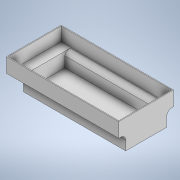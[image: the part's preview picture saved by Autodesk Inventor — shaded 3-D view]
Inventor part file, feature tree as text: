
AUTODESK INVENTOR PART (.ipt)
format: ipt  version: 2020.1 (Build 241239000, 239)  size: 161,792 bytes
history: native  units: mm
features: extrude x4, sketch x4, projected_geometry x4, other x1, fillet x1, shell x1
ambient origin geometry x8: Origin, YZ Plane, XZ Plane, XY Plane, X Axis, Y Axis, Z Axis, Center Point
bodies: Body1 (feature_tree)
feature tree (15):
  other  "Твердое тело1"
  extrude  "Выдавливание1"  Depth=142.0mm
  fillet  "Сопряжение1"  Radius=190.0mm
  extrude  "Выдавливание2"  Depth=50.0mm
  shell  "Оболочка1"  Thickness=24.0mm
  sketch  "Эскиз3"
  sketch  "Эскиз4"
  extrude  "Выдавливание3"  Depth=24.0mm
  extrude  "Выдавливание4"  Depth=50.0mm
  sketch  "Эскиз1"
  sketch  "Эскиз2"
  projected_geometry  "Спроецированная петля1"
  projected_geometry  "Спроецированная петля2"
  projected_geometry  "Спроецированная петля3"
  projected_geometry  "Спроецированная петля4"
